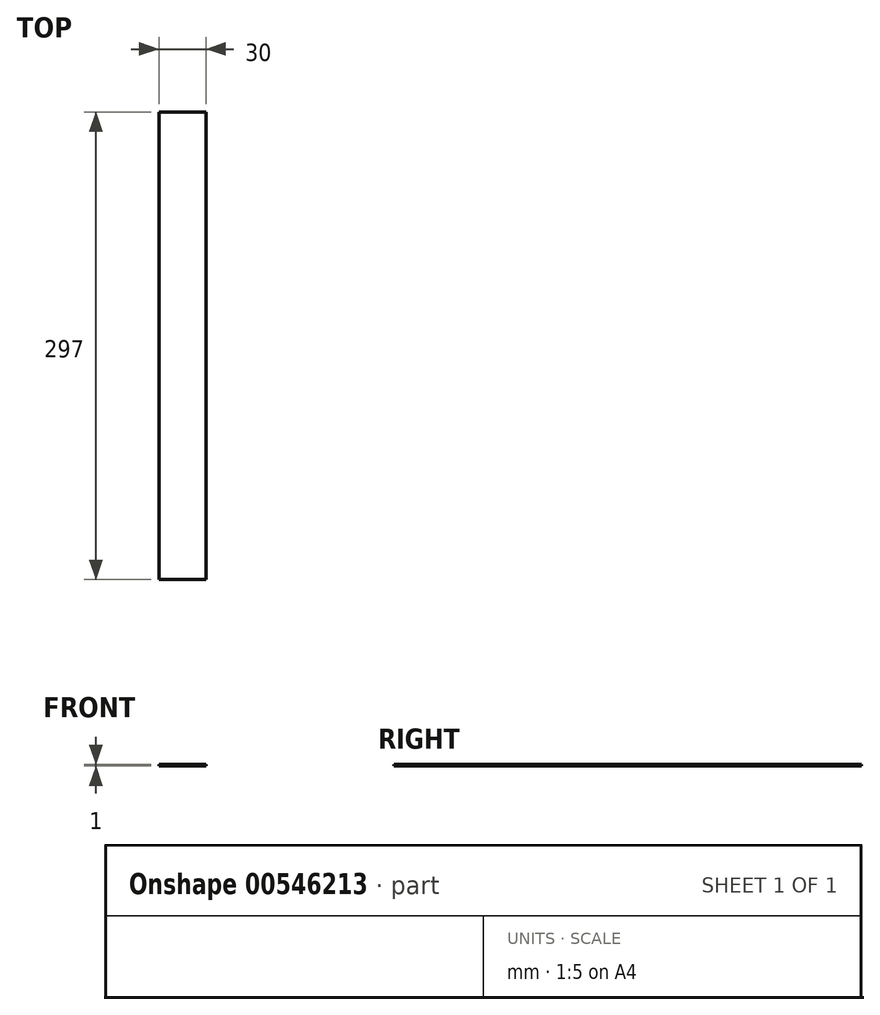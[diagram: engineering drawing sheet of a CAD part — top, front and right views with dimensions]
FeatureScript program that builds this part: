
annotation { "Feature Type Name" : "Feature", "Feature Type Description" : "" }
export const myFeature = defineFeature(function(context is Context, id is Id, definition is map)
    precondition{}
    {
        {
            var Q0;
            Q0=qCreatedBy(makeId("Top.planeOp"),FACE);
            var sketch = newSketch(context, id + "F0", { "sketchPlane" : qUnion([Q0])});
            skLineSegment(sketch, "E0.bottom", {"start": v(-15, 148.5) * mm, "end": v(15, 148.5) * mm});
            skLineSegment(sketch, "E0.top", {"start": v(-15, -148.5) * mm, "end": v(15, -148.5) * mm});
            skLineSegment(sketch, "E0.left", {"start": v(-15, 148.5) * mm, "end": v(-15, -148.5) * mm});
            skLineSegment(sketch, "E0.right", {"start": v(15, 148.5) * mm, "end": v(15, -148.5) * mm});
            skSolve(sketch);
        }
        {
            var Q0;
            Q0 = qSketchRegion(id + "F0", true);
            extrude(context, id + "F1", {"entities" : qUnion([Q0]), "endBound" : BoundingType.SYMMETRIC, "oppositeDirection" : true, "depth" : 1 * mm, "offsetDistance" : 25 * mm});
        }
    });
